# Revit family: РИДАН_Airvent_R_Воздухоотводчик
name_source: partatom
category: Арматура трубопроводов
units: mm (PartAtom-declared; Revit-internal decimal feet)

## family parameters
Всегда вертикально = Да
На основе рабочей плоскости = Нет
Общий = Нет
При загрузке вырезать с полостями = Нет
Размер круглого соединителя = Использовать диаметр
Тип детали = Нормальный

## types (2) — shared parameters
ADSK_Версия Revit = 2019
ADSK_Версия семейства = 1.0
ADSK_Диаметр условный = 15 мм
ADSK_Единица измерения = шт.
ADSK_Завод-изготовитель = ООО «Ридан-Трейд»
ADSK_Код изделия = 065B8322R
ADSK_Количество = 1
ADSK_Марка = Airvent-R
ADSK_Масса = 0.21
URL = https://ridan.ru
zero-valued in all types: УГО_Длина

## per-type parameters (varying)
| type | ADSK_Наименование | a | Обратный клапан |
| 065B8322R С обратным клапаном | Автоматический воздухоотводчик Airvent-R с обратным клапаном PN10, Tmax=110C | 19 мм | Да |
| 065B8323R Без обратного клапана | Автоматический воздухоотводчик Airvent-R без обратного клапана PN10, Tmax=110C | 0 мм | Нет |
